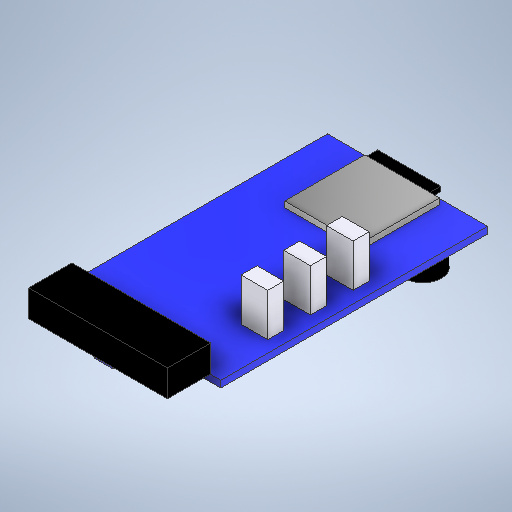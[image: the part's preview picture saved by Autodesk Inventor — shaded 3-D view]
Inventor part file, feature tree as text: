
AUTODESK INVENTOR PART (.ipt)
format: ipt  version: 2025.2 (Build 292293000, 293)  size: 353,792 bytes
history: native  units: mm
features: extrude x6, sketch x6
ambient origin geometry x8: Origin, YZ Plane, XZ Plane, XY Plane, X Axis, Y Axis, Z Axis, Center Point
bodies: Solid1 (feature_tree)
feature tree (12):
  extrude  "Extrusion1"  Depth=50.0mm
  extrude  "Extrusion2"  Depth=7.0mm
  extrude  "Extrusion3"  Depth=1.25mm TaperAngle=0.0deg
  extrude  "Extrusion4"  Depth=8.1mm
  extrude  "Extrusion5"  Depth=2.0mm
  extrude  "Extrusion6"  Depth=5.0mm
  sketch  "Sketch1"  dims[d0=30.0mm d1=50.0mm]
  sketch  "Sketch2"  dims[d2=7.0mm d3=1.75mm]
  sketch  "Sketch3"  dims[d4=3.5mm d5=1.25mm d6=0.0mm]
  sketch  "Sketch4"  dims[d7=1.0mm d8=8.1mm]
  sketch  "Sketch5"  dims[d9=2.0mm d10=2.0mm]
  sketch  "Sketch6"  dims[d11=5.0mm d12=0.0mm d13=5.0mm d14=3.0mm d15=5.0mm d16=3.0mm d17=5.0mm d18=3.0mm d19=2.2mm d20=2.2mm d21=2.2mm d22=20.0mm d23=5.0mm d24=5.0mm d25=8.0mm d26=0.0mm d27=8.0mm d28=8.0mm d29=1.0mm d30=15.0mm d31=1.1mm d32=0.0mm d33=2.0mm d34=0.2mm d35=0.2mm d36=0.017mm d37=2.2mm d38=0.0mm d39=7.0mm d40=7.0mm d41=8.5mm d42=8.5mm d43=3.6mm d44=3.6mm d45=3.0mm d46=0.0mm]
